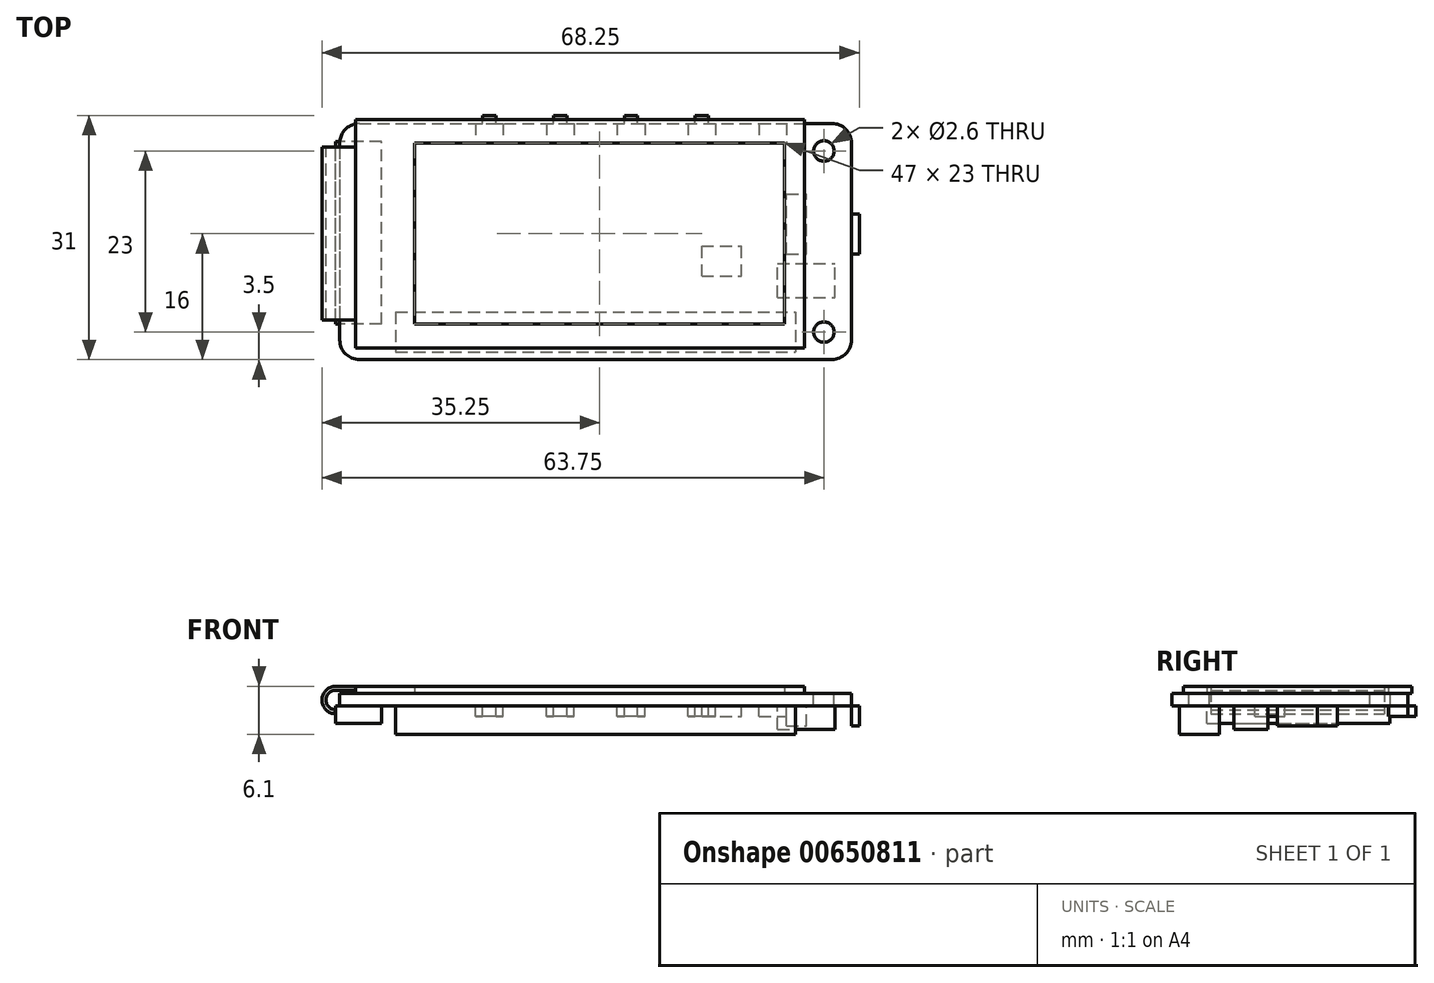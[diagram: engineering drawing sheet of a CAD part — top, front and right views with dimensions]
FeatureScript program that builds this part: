
annotation { "Feature Type Name" : "Feature", "Feature Type Description" : "" }
export const myFeature = defineFeature(function(context is Context, id is Id, definition is map)
    precondition{}
    {
        {
            var Q0;
            Q0=qCreatedBy(makeId("Top.planeOp"),FACE);
            var sketch = newSketch(context, id + "F0", { "sketchPlane" : qUnion([Q0])});
            skLineSegment(sketch, "E0.bottom", {"start": v(-30, 15) * mm, "end": v(30, 15) * mm});
            skLineSegment(sketch, "E0.top", {"start": v(-30, -15) * mm, "end": v(30, -15) * mm});
            skLineSegment(sketch, "E0.left", {"start": v(-32.5, 12.5) * mm, "end": v(-32.5, -12.5) * mm});
            skLineSegment(sketch, "E0.right", {"start": v(32.5, 12.5) * mm, "end": v(32.5, -12.5) * mm});
            skPoint(sketch, "E0.middle", {"position": v(0, 0) * mm});
            skPoint(sketch, "E1.visualSharp", {"position": v(-32.5, 15) * mm});
            skArc(sketch, "E1.filletArc", {"start": v(-30, 15) * mm, "mid": v(-31.77, 14.27) * mm, "end": v(-32.5, 12.5) * mm});
            skPoint(sketch, "E2.visualSharp", {"position": v(32.5, 15) * mm});
            skArc(sketch, "E2.filletArc", {"start": v(32.5, 12.5) * mm, "mid": v(31.77, 14.27) * mm, "end": v(30, 15) * mm});
            skPoint(sketch, "E3.visualSharp", {"position": v(32.5, -15) * mm});
            skArc(sketch, "E3.filletArc", {"start": v(30, -15) * mm, "mid": v(31.77, -14.27) * mm, "end": v(32.5, -12.5) * mm});
            skPoint(sketch, "E4.visualSharp", {"position": v(-32.5, -15) * mm});
            skArc(sketch, "E4.filletArc", {"start": v(-32.5, -12.5) * mm, "mid": v(-31.77, -14.27) * mm, "end": v(-30, -15) * mm});
            skLineSegment(sketch, "E5.bottom", {"start": v(-29, 11.5) * mm, "end": v(29, 11.5) * mm, "construction": true});
            skLineSegment(sketch, "E5.top", {"start": v(-29, -11.5) * mm, "end": v(29, -11.5) * mm, "construction": true});
            skLineSegment(sketch, "E5.left", {"start": v(-29, 11.5) * mm, "end": v(-29, -11.5) * mm, "construction": true});
            skLineSegment(sketch, "E5.right", {"start": v(29, 11.5) * mm, "end": v(29, -11.5) * mm, "construction": true});
            skCircle(sketch, "E6", {"center": v(29, 11.5) * mm, "radius": 1.3 * mm});
            skCircle(sketch, "E7", {"center": v(29, -11.5) * mm, "radius": 1.3 * mm});
            skSolve(sketch);
        }
        {
            var Q0;
            Q0=makeQuery(id+"F0.imprint","IMPRINT",FACE,{"disambiguationData":[TD([[makeQuery(id+"F0.imprint","IMPRINT",EDGE,{"derivedFrom":sQuery(id+"F0.wireOp",EDGE,"E0.bottom")}),-1.0]])]});
            extrude(context, id + "F1", {"entities" : qUnion([Q0]), "oppositeDirection" : true, "depth" : 1.6 * mm, "offsetDistance" : 25 * mm});
        }
        {
            var Q0;
            Q0=qCreatedBy(makeId("Top.planeOp"),FACE);
            var sketch = newSketch(context, id + "F2", { "sketchPlane" : qUnion([Q0])});
            skLineSegment(sketch, "E8.bottom", {"start": v(-30.5, 15.5) * mm, "end": v(26.5, 15.5) * mm});
            skLineSegment(sketch, "E8.top", {"start": v(-30.5, -13.5) * mm, "end": v(26.5, -13.5) * mm});
            skLineSegment(sketch, "E8.left", {"start": v(-30.5, 15.5) * mm, "end": v(-30.5, -13.5) * mm});
            skLineSegment(sketch, "E8.right", {"start": v(26.5, 15.5) * mm, "end": v(26.5, -13.5) * mm});
            skLineSegment(sketch, "E9.bottom", {"start": v(-23, 12.5) * mm, "end": v(24, 12.5) * mm});
            skLineSegment(sketch, "E9.top", {"start": v(-23, -10.5) * mm, "end": v(24, -10.5) * mm});
            skLineSegment(sketch, "E9.left", {"start": v(-23, 12.5) * mm, "end": v(-23, -10.5) * mm});
            skLineSegment(sketch, "E9.right", {"start": v(24, 12.5) * mm, "end": v(24, -10.5) * mm});
            skSolve(sketch);
        }
        {
            var Q0;
            Q0=makeQuery(id+"F2.imprint","IMPRINT",FACE,{"disambiguationData":[TD([[makeQuery(id+"F2.imprint","IMPRINT",EDGE,{"derivedFrom":sQuery(id+"F2.wireOp",EDGE,"E9.bottom")}),-1.0]])]});
            extrude(context, id + "F3", {"entities" : qUnion([Q0]), "depth" : 0.9 * mm, "offsetDistance" : 25 * mm});
        }
        {
            var Q0;
            Q0=makeQuery(id+"F2.imprint","IMPRINT",FACE,{"disambiguationData":[TD([[makeQuery(id+"F2.imprint","IMPRINT",EDGE,{"derivedFrom":sQuery(id+"F2.wireOp",EDGE,"E8.bottom")}),-1.0]])]});
            extrude(context, id + "F4", {"entities" : qUnion([Q0]), "depth" : 0.9 * mm, "offsetDistance" : 25 * mm});
        }
        {
            var Q0;
            Q0=makeQuery(id+"F1.opExtrude","CAP_FACE",FACE,{"disambiguationData":[OSD([sQuery(id+"F0.wireOp",EDGE,"E0.bottom"),sQuery(id+"F0.wireOp",EDGE,"E0.top"),sQuery(id+"F0.wireOp",EDGE,"E0.left"),sQuery(id+"F0.wireOp",EDGE,"E0.right"),sQuery(id+"F0.wireOp",EDGE,"E1.filletArc"),sQuery(id+"F0.wireOp",EDGE,"E2.filletArc"),sQuery(id+"F0.wireOp",EDGE,"E3.filletArc"),sQuery(id+"F0.wireOp",EDGE,"E4.filletArc"),sQuery(id+"F0.wireOp",EDGE,"E6"),sQuery(id+"F0.wireOp",EDGE,"E7")])],"isStart":false});
            var sketch = newSketch(context, id + "F5", { "sketchPlane" : qUnion([Q0])});
            skLineSegment(sketch, "E10.bottom", {"start": v(-25.4, 8.96) * mm, "end": v(25.4, 8.96) * mm});
            skLineSegment(sketch, "E10.top", {"start": v(-25.4, 14.04) * mm, "end": v(25.4, 14.04) * mm});
            skLineSegment(sketch, "E10.left", {"start": v(-25.4, 8.96) * mm, "end": v(-25.4, 14.04) * mm});
            skLineSegment(sketch, "E10.right", {"start": v(25.4, 8.96) * mm, "end": v(25.4, 14.04) * mm});
            skPoint(sketch, "E10.middle", {"position": v(0, 11.5) * mm});
            skLineSegment(sketch, "E11.bottom", {"start": v(24.25, -15) * mm, "end": v(20.75, -15) * mm});
            skLineSegment(sketch, "E11.top", {"start": v(24.25, -12.5) * mm, "end": v(20.75, -12.5) * mm});
            skLineSegment(sketch, "E11.left", {"start": v(24.25, -15) * mm, "end": v(24.25, -12.5) * mm});
            skLineSegment(sketch, "E11.right", {"start": v(20.75, -15) * mm, "end": v(20.75, -12.5) * mm});
            skPoint(sketch, "E11.middle", {"position": v(22.5, -13.75) * mm});
            skLineSegment(sketch, "E12.bottom", {"start": v(23.35, -15) * mm, "end": v(21.65, -15) * mm});
            skLineSegment(sketch, "E12.top", {"start": v(23.35, -16) * mm, "end": v(21.65, -16) * mm});
            skLineSegment(sketch, "E12.left", {"start": v(23.35, -15) * mm, "end": v(23.35, -16) * mm});
            skLineSegment(sketch, "E12.right", {"start": v(21.65, -15) * mm, "end": v(21.65, -16) * mm});
            skPoint(sketch, "E12.middle", {"position": v(22.5, -15.5) * mm});
            skLineSegment(sketch, "E13", {"start": v(22.5, -15.5) * mm, "end": v(22.5, -13.75) * mm, "construction": true});
            skLineSegment(sketch, "E14.1.0.0", {"start": v(15.25, -15) * mm, "end": v(15.25, -12.5) * mm});
            skLineSegment(sketch, "E14.1.0.1", {"start": v(15.25, -12.5) * mm, "end": v(11.75, -12.5) * mm});
            skLineSegment(sketch, "E14.1.0.2", {"start": v(15.25, -15) * mm, "end": v(11.75, -15) * mm});
            skLineSegment(sketch, "E14.1.0.3", {"start": v(11.75, -15) * mm, "end": v(11.75, -12.5) * mm});
            skLineSegment(sketch, "E14.1.0.4", {"start": v(12.65, -15) * mm, "end": v(12.65, -16) * mm});
            skLineSegment(sketch, "E14.1.0.5", {"start": v(14.35, -16) * mm, "end": v(12.65, -16) * mm});
            skLineSegment(sketch, "E14.1.0.6", {"start": v(14.35, -15) * mm, "end": v(14.35, -16) * mm});
            skLineSegment(sketch, "E14.2.0.0", {"start": v(6.25, -15) * mm, "end": v(6.25, -12.5) * mm});
            skLineSegment(sketch, "E14.2.0.1", {"start": v(6.25, -12.5) * mm, "end": v(2.75, -12.5) * mm});
            skLineSegment(sketch, "E14.2.0.2", {"start": v(6.25, -15) * mm, "end": v(2.75, -15) * mm});
            skLineSegment(sketch, "E14.2.0.3", {"start": v(2.75, -15) * mm, "end": v(2.75, -12.5) * mm});
            skLineSegment(sketch, "E14.2.0.4", {"start": v(3.65, -15) * mm, "end": v(3.65, -16) * mm});
            skLineSegment(sketch, "E14.2.0.5", {"start": v(5.35, -16) * mm, "end": v(3.65, -16) * mm});
            skLineSegment(sketch, "E14.2.0.6", {"start": v(5.35, -15) * mm, "end": v(5.35, -16) * mm});
            skLineSegment(sketch, "E14.3.0.0", {"start": v(-2.75, -15) * mm, "end": v(-2.75, -12.5) * mm});
            skLineSegment(sketch, "E14.3.0.1", {"start": v(-2.75, -12.5) * mm, "end": v(-6.25, -12.5) * mm});
            skLineSegment(sketch, "E14.3.0.2", {"start": v(-2.75, -15) * mm, "end": v(-6.25, -15) * mm});
            skLineSegment(sketch, "E14.3.0.3", {"start": v(-6.25, -15) * mm, "end": v(-6.25, -12.5) * mm});
            skLineSegment(sketch, "E14.3.0.4", {"start": v(-5.35, -15) * mm, "end": v(-5.35, -16) * mm});
            skLineSegment(sketch, "E14.3.0.5", {"start": v(-3.65, -16) * mm, "end": v(-5.35, -16) * mm});
            skLineSegment(sketch, "E14.3.0.6", {"start": v(-3.65, -15) * mm, "end": v(-3.65, -16) * mm});
            skLineSegment(sketch, "E14.4.0.0", {"start": v(-11.75, -15) * mm, "end": v(-11.75, -12.5) * mm});
            skLineSegment(sketch, "E14.4.0.1", {"start": v(-11.75, -12.5) * mm, "end": v(-15.25, -12.5) * mm});
            skLineSegment(sketch, "E14.4.0.2", {"start": v(-11.75, -15) * mm, "end": v(-15.25, -15) * mm});
            skLineSegment(sketch, "E14.4.0.3", {"start": v(-15.25, -15) * mm, "end": v(-15.25, -12.5) * mm});
            skLineSegment(sketch, "E14.4.0.4", {"start": v(-14.35, -15) * mm, "end": v(-14.35, -16) * mm});
            skLineSegment(sketch, "E14.4.0.5", {"start": v(-12.65, -16) * mm, "end": v(-14.35, -16) * mm});
            skLineSegment(sketch, "E14.4.0.6", {"start": v(-12.65, -15) * mm, "end": v(-12.65, -16) * mm});
            skLineSegment(sketch, "E14.direction1", {"start": v(24.25, -15) * mm, "end": v(15.25, -15) * mm, "construction": true});
            skLineSegment(sketch, "E15.bottom", {"start": v(13.5, 4.4) * mm, "end": v(18.5, 4.4) * mm});
            skLineSegment(sketch, "E15.top", {"start": v(13.5, 0.6) * mm, "end": v(18.5, 0.6) * mm});
            skLineSegment(sketch, "E15.left", {"start": v(13.5, 4.4) * mm, "end": v(13.5, 0.6) * mm});
            skLineSegment(sketch, "E15.right", {"start": v(18.5, 4.4) * mm, "end": v(18.5, 0.6) * mm});
            skLineSegment(sketch, "E16.bottom", {"start": v(23.1, 7.1) * mm, "end": v(30.4, 7.1) * mm});
            skLineSegment(sketch, "E16.top", {"start": v(23.1, 2.8) * mm, "end": v(30.4, 2.8) * mm});
            skLineSegment(sketch, "E16.left", {"start": v(23.1, 7.1) * mm, "end": v(23.1, 2.8) * mm});
            skLineSegment(sketch, "E16.right", {"start": v(30.4, 7.1) * mm, "end": v(30.4, 2.8) * mm});
            skLineSegment(sketch, "E17.bottom", {"start": v(24.26, 1.6) * mm, "end": v(26.8, 1.6) * mm});
            skLineSegment(sketch, "E17.top", {"start": v(24.26, -6.02) * mm, "end": v(26.8, -6.02) * mm});
            skLineSegment(sketch, "E17.left", {"start": v(24.26, 1.6) * mm, "end": v(24.26, -6.02) * mm});
            skLineSegment(sketch, "E17.right", {"start": v(26.8, 1.6) * mm, "end": v(26.8, -6.02) * mm});
            skLineSegment(sketch, "E18.bottom", {"start": v(26.8, 1.6) * mm, "end": v(33.5, 1.6) * mm});
            skLineSegment(sketch, "E18.top", {"start": v(26.8, -3.48) * mm, "end": v(33.5, -3.48) * mm});
            skLineSegment(sketch, "E18.left", {"start": v(26.8, 1.6) * mm, "end": v(26.8, -3.48) * mm});
            skLineSegment(sketch, "E18.right", {"start": v(33.5, 1.6) * mm, "end": v(33.5, -3.48) * mm});
            skLineSegment(sketch, "E19.bottom", {"start": v(-27.2, 10.5) * mm, "end": v(-33, 10.5) * mm});
            skLineSegment(sketch, "E19.top", {"start": v(-27.2, -12.7) * mm, "end": v(-33, -12.7) * mm});
            skLineSegment(sketch, "E19.left", {"start": v(-27.2, 10.5) * mm, "end": v(-27.2, -12.7) * mm});
            skLineSegment(sketch, "E19.right", {"start": v(-33, 10.5) * mm, "end": v(-33, -12.7) * mm});
            skSolve(sketch);
        }
        {
            var Q0;
            Q0=makeQuery(id+"F5.imprint","IMPRINT",FACE,{"disambiguationData":[TD([[makeQuery(id+"F5.imprint","IMPRINT",EDGE,{"derivedFrom":sQuery(id+"F5.wireOp",EDGE,"E15.bottom")}),-1.0]])]});
            var Q1;
            Q1=makeQuery(id+"F5.imprint","IMPRINT",FACE,{"disambiguationData":[TD([[makeQuery(id+"F5.imprint","IMPRINT",EDGE,{"derivedFrom":sQuery(id+"F5.wireOp",EDGE,"E11.top")}),1.0]])]});
            var Q2;
            {var subQ5=sQuery(id+"F5.wireOp",EDGE,"E14.1.0.0");Q2=makeQuery(id+"F5.imprint","IMPRINT",FACE,{"disambiguationData":[TD([[makeQuery(id+"F5.imprint","IMPRINT",EDGE,{"derivedFrom":subQ5}),1.0]])]});}
            var Q3;
            {var subQ5=sQuery(id+"F5.wireOp",EDGE,"E14.2.0.0");Q3=makeQuery(id+"F5.imprint","IMPRINT",FACE,{"disambiguationData":[TD([[makeQuery(id+"F5.imprint","IMPRINT",EDGE,{"derivedFrom":subQ5}),1.0]])]});}
            var Q4;
            {var subQ5=sQuery(id+"F5.wireOp",EDGE,"E14.3.0.0");Q4=makeQuery(id+"F5.imprint","IMPRINT",FACE,{"disambiguationData":[TD([[makeQuery(id+"F5.imprint","IMPRINT",EDGE,{"derivedFrom":subQ5}),1.0]])]});}
            var Q5;
            {var subQ5=sQuery(id+"F5.wireOp",EDGE,"E14.4.0.0");Q5=makeQuery(id+"F5.imprint","IMPRINT",FACE,{"disambiguationData":[TD([[makeQuery(id+"F5.imprint","IMPRINT",EDGE,{"derivedFrom":subQ5}),1.0]])]});}
            var Q6;
            {var subQ0=sQuery(id+"F5.wireOp",EDGE,"E14.4.0.4");Q6=makeQuery(id+"F5.imprint","IMPRINT",FACE,{"disambiguationData":[TD([[makeQuery(id+"F5.imprint","IMPRINT",EDGE,{"derivedFrom":subQ0}),1.0]])]});}
            var Q7;
            {var subQ0=sQuery(id+"F5.wireOp",EDGE,"E14.3.0.4");Q7=makeQuery(id+"F5.imprint","IMPRINT",FACE,{"disambiguationData":[TD([[makeQuery(id+"F5.imprint","IMPRINT",EDGE,{"derivedFrom":subQ0}),1.0]])]});}
            var Q8;
            {var subQ0=sQuery(id+"F5.wireOp",EDGE,"E14.2.0.4");Q8=makeQuery(id+"F5.imprint","IMPRINT",FACE,{"disambiguationData":[TD([[makeQuery(id+"F5.imprint","IMPRINT",EDGE,{"derivedFrom":subQ0}),1.0]])]});}
            var Q9;
            {var subQ0=sQuery(id+"F5.wireOp",EDGE,"E14.1.0.4");Q9=makeQuery(id+"F5.imprint","IMPRINT",FACE,{"disambiguationData":[TD([[makeQuery(id+"F5.imprint","IMPRINT",EDGE,{"derivedFrom":subQ0}),1.0]])]});}
            var Q10;
            Q10=makeQuery(id+"F5.imprint","IMPRINT",FACE,{"disambiguationData":[TD([[makeQuery(id+"F5.imprint","IMPRINT",EDGE,{"derivedFrom":sQuery(id+"F5.wireOp",EDGE,"E12.bottom")}),-1.0]])]});
            extrude(context, id + "F6", {"entities" : qUnion([Q0, Q1, Q2, Q3, Q4, Q5, Q6, Q7, Q8, Q9, Q10]), "depth" : 1.3 * mm, "offsetDistance" : 25 * mm});
        }
        {
            var Q0;
            {var subQ5=sQuery(id+"F5.wireOp",EDGE,"E19.left");Q0=makeQuery(id+"F5.imprint","IMPRINT",FACE,{"disambiguationData":[TD([[makeQuery(id+"F5.imprint","IMPRINT",EDGE,{"derivedFrom":subQ5}),-1.0]])]});}
            var Q1;
            {var subQ5=sQuery(id+"F5.wireOp",EDGE,"E19.right");Q1=makeQuery(id+"F5.imprint","IMPRINT",FACE,{"disambiguationData":[TD([[makeQuery(id+"F5.imprint","IMPRINT",EDGE,{"derivedFrom":subQ5}),1.0]])]});}
            extrude(context, id + "F7", {"entities" : qUnion([Q0, Q1]), "depth" : 2.2 * mm, "offsetDistance" : 25 * mm});
        }
        {
            var Q0;
            {var subQ0=sQuery(id+"F5.wireOp",EDGE,"E18.left");Q0=makeQuery(id+"F5.imprint","IMPRINT",FACE,{"disambiguationData":[TD([[makeQuery(id+"F5.imprint","IMPRINT",EDGE,{"derivedFrom":subQ0}),1.0]])]});}
            var Q1;
            Q1=makeQuery(id+"F5.imprint","IMPRINT",FACE,{"disambiguationData":[TD([[makeQuery(id+"F5.imprint","IMPRINT",EDGE,{"derivedFrom":sQuery(id+"F5.wireOp",EDGE,"E17.bottom")}),-1.0]])]});
            var Q2;
            {var subQ0=sQuery(id+"F5.wireOp",EDGE,"E18.right");Q2=makeQuery(id+"F5.imprint","IMPRINT",FACE,{"disambiguationData":[TD([[makeQuery(id+"F5.imprint","IMPRINT",EDGE,{"derivedFrom":subQ0}),-1.0]])]});}
            extrude(context, id + "F8", {"entities" : qUnion([Q0, Q1, Q2]), "depth" : 2.54 * mm, "offsetDistance" : 25 * mm});
        }
        {
            var Q0;
            Q0=makeQuery(id+"F5.imprint","IMPRINT",FACE,{"disambiguationData":[TD([[makeQuery(id+"F5.imprint","IMPRINT",EDGE,{"derivedFrom":sQuery(id+"F5.wireOp",EDGE,"E16.bottom")}),-1.0]])]});
            extrude(context, id + "F9", {"entities" : qUnion([Q0]), "depth" : 3 * mm, "offsetDistance" : 25 * mm});
        }
        {
            var Q0;
            Q0=makeQuery(id+"F5.imprint","IMPRINT",FACE,{"disambiguationData":[TD([[makeQuery(id+"F5.imprint","IMPRINT",EDGE,{"derivedFrom":sQuery(id+"F5.wireOp",EDGE,"E10.bottom")}),1.0]])]});
            extrude(context, id + "F10", {"entities" : qUnion([Q0]), "depth" : 3.6 * mm, "offsetDistance" : 25 * mm});
        }
        {
            var Q0;
            Q0=qCreatedBy(makeId("Front.planeOp"),FACE);
            var sketch = newSketch(context, id + "F11", { "sketchPlane" : qUnion([Q0])});
            skLineSegment(sketch, "E20", {"start": v(-30.5, 0.9) * mm, "end": v(-33, 0.9) * mm});
            skLineSegment(sketch, "E21", {"start": v(-30.5, 0.9) * mm, "end": v(-30.5, 0.4) * mm});
            skLineSegment(sketch, "E22", {"start": v(-30.5, 0.4) * mm, "end": v(-33, 0.4) * mm});
            skArc(sketch, "E23", {"start": v(-33, 0.4) * mm, "mid": v(-34.25, -0.85) * mm, "end": v(-33, -2.1) * mm});
            skArc(sketch, "E24", {"start": v(-33, 0.9) * mm, "mid": v(-34.75, -0.85) * mm, "end": v(-33, -2.6) * mm});
            skLineSegment(sketch, "E25", {"start": v(-33, -2.1) * mm, "end": v(-33, -2.6) * mm});
            skSolve(sketch);
        }
        {
            var Q0;
            Q0=makeQuery(id+"F11.imprint","IMPRINT",FACE,{"disambiguationData":[TD([[makeQuery(id+"F11.imprint","IMPRINT",EDGE,{"derivedFrom":sQuery(id+"F11.wireOp",EDGE,"E20")}),1.0]])]});
            extrude(context, id + "F12", {"entities" : qUnion([Q0]), "depth" : 10 * mm, "offsetDistance" : 25 * mm, "hasSecondDirection" : true, "secondDirectionOppositeDirection" : true, "secondDirectionDepth" : 12 * mm});
        }
    });
